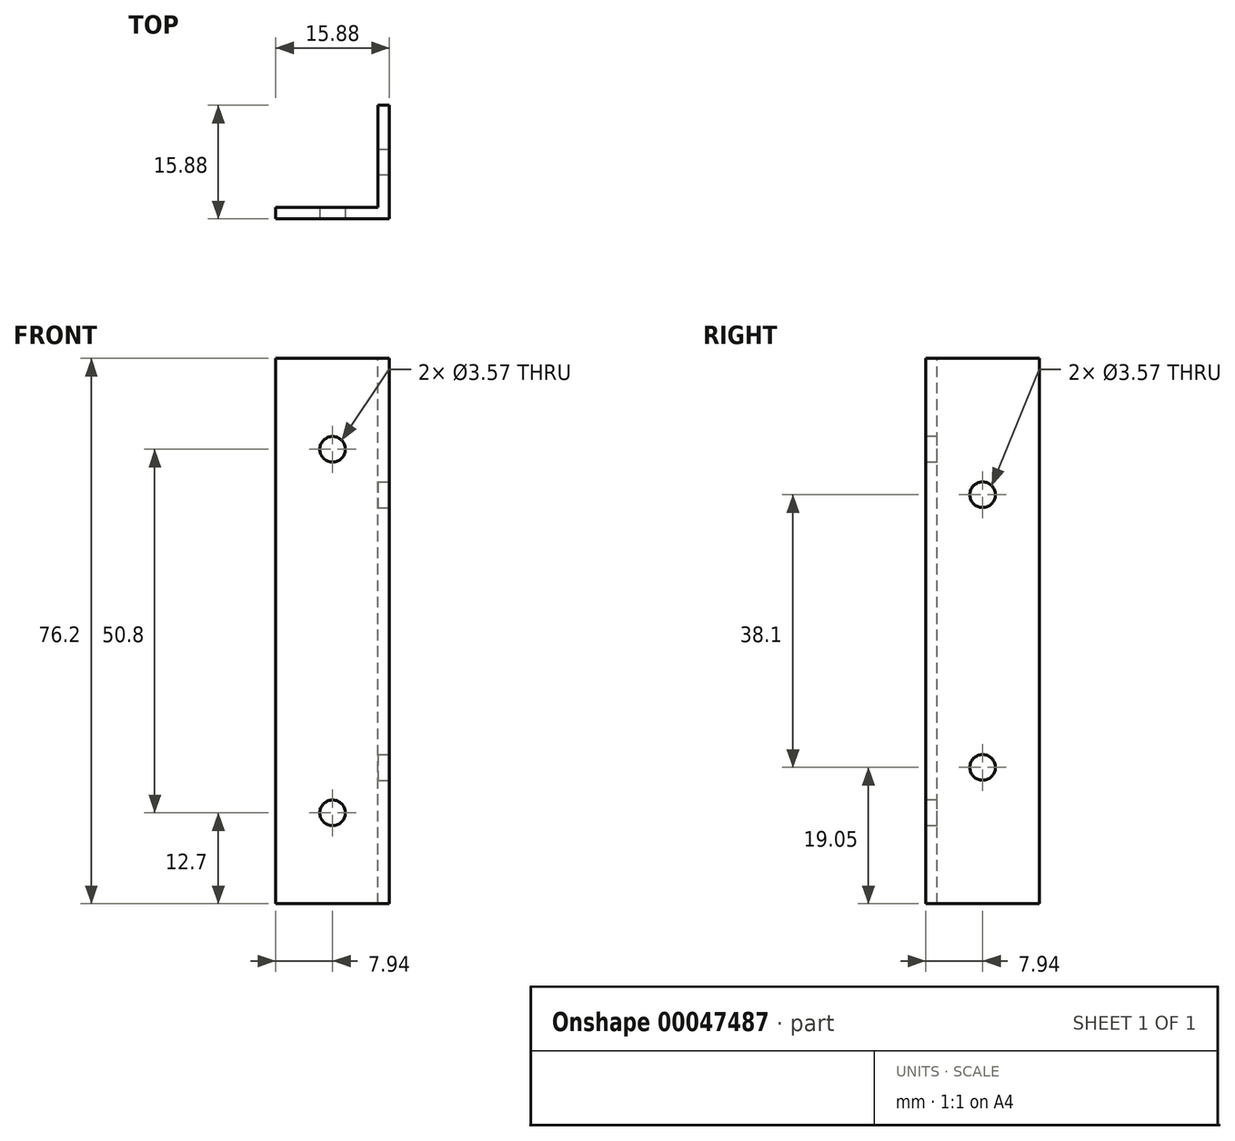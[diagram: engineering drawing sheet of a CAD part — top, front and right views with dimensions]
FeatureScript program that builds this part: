
annotation { "Feature Type Name" : "Feature", "Feature Type Description" : "" }
export const myFeature = defineFeature(function(context is Context, id is Id, definition is map)
    precondition{}
    {
        {
            var Q0;
            Q0=qCreatedBy(makeId("Top.planeOp"),FACE);
            var sketch = newSketch(context, id + "F0", { "sketchPlane" : qUnion([Q0])});
            skLineSegment(sketch, "E0.rect.bottom", {"start": v(-7.94, 7.94) * mm, "end": v(7.94, 7.94) * mm});
            skLineSegment(sketch, "E0.rect.top", {"start": v(-7.94, -7.94) * mm, "end": v(7.94, -7.94) * mm});
            skLineSegment(sketch, "E0.rect.left", {"start": v(-7.94, 7.94) * mm, "end": v(-7.94, -7.94) * mm});
            skLineSegment(sketch, "E0.rect.right", {"start": v(7.94, 7.94) * mm, "end": v(7.94, -7.94) * mm});
            skPoint(sketch, "E0.rect.middle", {"position": v(0, 0) * mm});
            skSolve(sketch);
        }
        {
            var Q0;
            Q0 = qSketchRegion(id + "F0", true);
            extrude(context, id + "F1", {"entities" : qUnion([Q0]), "depth" : 76.2 * mm, "symmetric" : true});
        }
        {
            var Q0;
            Q0=makeQuery(id+"F1.opExtrude","CAP_FACE",FACE,{"disambiguationData":[OSD([sQuery(id+"F0.wireOp",EDGE,"E0.rect.bottom"),sQuery(id+"F0.wireOp",EDGE,"E0.rect.top"),sQuery(id+"F0.wireOp",EDGE,"E0.rect.left"),sQuery(id+"F0.wireOp",EDGE,"E0.rect.right")])],"isStart":false});
            var sketch = newSketch(context, id + "F2", { "sketchPlane" : qUnion([Q0])});
            skLineSegment(sketch, "E1.bottom", {"start": v(-7.94, 7.94) * mm, "end": v(6.35, 7.94) * mm});
            skLineSegment(sketch, "E1.top", {"start": v(-7.94, -6.35) * mm, "end": v(6.35, -6.35) * mm});
            skLineSegment(sketch, "E1.left", {"start": v(-7.94, 7.94) * mm, "end": v(-7.94, -6.35) * mm});
            skLineSegment(sketch, "E1.right", {"start": v(6.35, 7.94) * mm, "end": v(6.35, -6.35) * mm});
            skSolve(sketch);
        }
        {
            var Q0;
            Q0=makeQuery(id+"F2.imprint","IMPRINT",FACE,{"disambiguationData":[TD([[makeQuery(id+"F2.imprint","IMPRINT",EDGE,{"derivedFrom":sQuery(id+"F2.wireOp",EDGE,"E1.bottom")}),-1.0]])]});
            extrude(context, id + "F3", {"entities" : qUnion([Q0]), "operationType" : NewBodyOperationType.REMOVE, "oppositeDirection" : true, "depth" : 76.2 * mm});
        }
        {
            var Q0;
            Q0=makeQuery(id+"F1.opExtrude","SWEPT_FACE",FACE,{"disambiguationData":[OSD([sQuery(id+"F0.wireOp",EDGE,"E0.rect.top")])]});
            var sketch = newSketch(context, id + "F4", { "sketchPlane" : qUnion([Q0])});
            skCircle(sketch, "E2", {"center": v(0, -25.4) * mm, "radius": 1.79 * mm});
            skCircle(sketch, "E3", {"center": v(0, 25.4) * mm, "radius": 1.79 * mm});
            skSolve(sketch);
        }
        {
            var Q0;
            Q0 = qSketchRegion(id + "F4", true);
            var Q1;
            Q1=makeQuery(id+"F3.boolean.opBoolean","COPY",FACE,{"derivedFrom":makeQuery(id+"F3.opExtrude","SWEPT_FACE",FACE,{"disambiguationData":[OSD([sQuery(id+"F2.wireOp",EDGE,"E1.top")])]})});
            extrude(context, id + "F5", {"entities" : qUnion([Q0]), "operationType" : NewBodyOperationType.REMOVE, "endBound" : BoundingType.UP_TO_SURFACE, "oppositeDirection" : true, "endBoundEntityFace" : qUnion([Q1]), "depth" : 25.4 * mm});
        }
        {
            var Q0;
            Q0=makeQuery(id+"F1.opExtrude","SWEPT_FACE",FACE,{"disambiguationData":[OSD([sQuery(id+"F0.wireOp",EDGE,"E0.rect.right")])]});
            var sketch = newSketch(context, id + "F6", { "sketchPlane" : qUnion([Q0])});
            skCircle(sketch, "E4", {"center": v(0, -19.05) * mm, "radius": 1.79 * mm});
            skCircle(sketch, "E5", {"center": v(0, 19.05) * mm, "radius": 1.79 * mm});
            skSolve(sketch);
        }
        {
            var Q0;
            Q0 = qSketchRegion(id + "F6", true);
            var Q1;
            Q1=makeQuery(id+"F3.boolean.opBoolean","COPY",FACE,{"derivedFrom":makeQuery(id+"F3.opExtrude","SWEPT_FACE",FACE,{"disambiguationData":[OSD([sQuery(id+"F2.wireOp",EDGE,"E1.right")])]})});
            extrude(context, id + "F7", {"entities" : qUnion([Q0]), "operationType" : NewBodyOperationType.REMOVE, "endBound" : BoundingType.UP_TO_SURFACE, "oppositeDirection" : true, "endBoundEntityFace" : qUnion([Q1]), "depth" : 25.4 * mm});
        }
    });
